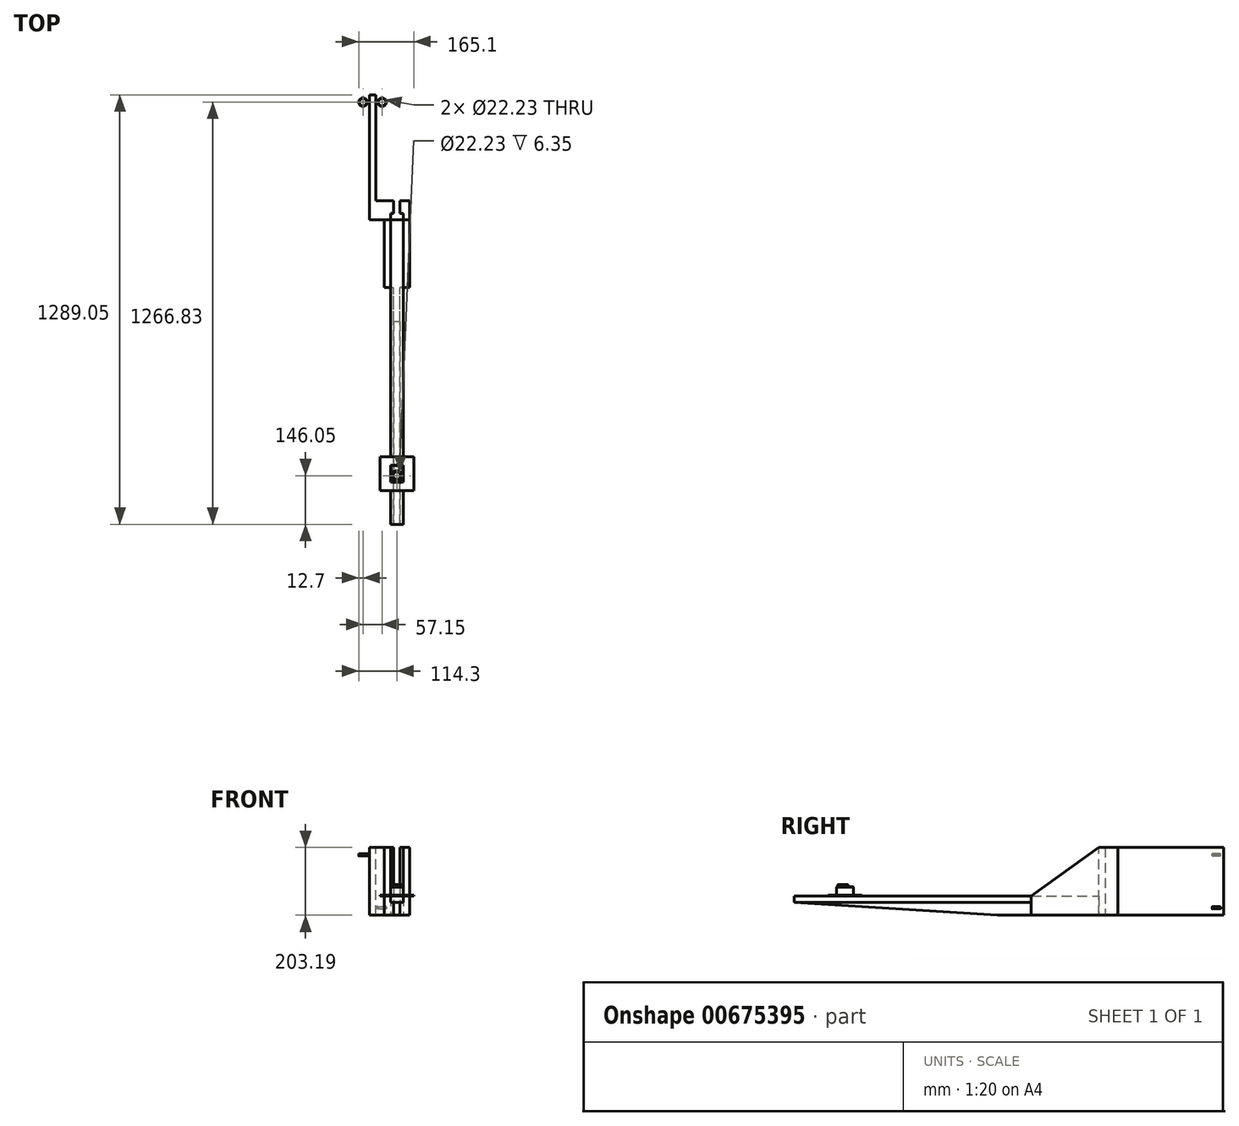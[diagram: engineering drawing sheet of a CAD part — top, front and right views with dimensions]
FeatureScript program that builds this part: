
annotation { "Feature Type Name" : "Feature", "Feature Type Description" : "" }
export const myFeature = defineFeature(function(context is Context, id is Id, definition is map)
    precondition{}
    {
        {
            var Q0;
            Q0=qCreatedBy(makeId("Front.planeOp"),FACE);
            var sketch = newSketch(context, id + "F0", { "sketchPlane" : qUnion([Q0])});
            skLineSegment(sketch, "E0.bottom", {"start": v(-19.05, 9.52) * mm, "end": v(19.05, 9.52) * mm});
            skLineSegment(sketch, "E0.top", {"start": v(-19.05, -9.53) * mm, "end": v(19.05, -9.53) * mm});
            skLineSegment(sketch, "E0.left", {"start": v(-19.05, 9.53) * mm, "end": v(-19.05, -9.53) * mm});
            skLineSegment(sketch, "E0.right", {"start": v(19.05, 9.53) * mm, "end": v(19.05, -9.53) * mm});
            skLineSegment(sketch, "E1.bottom", {"start": v(-9.52, -9.53) * mm, "end": v(9.53, -9.53) * mm});
            skLineSegment(sketch, "E1.top", {"start": v(-9.52, -47.62) * mm, "end": v(9.53, -47.62) * mm});
            skLineSegment(sketch, "E1.left", {"start": v(-9.52, -9.53) * mm, "end": v(-9.52, -47.62) * mm});
            skLineSegment(sketch, "E1.right", {"start": v(9.53, -9.52) * mm, "end": v(9.53, -47.62) * mm});
            skSolve(sketch);
        }
        {
            var Q0;
            Q0 = qSketchRegion(id + "F0", true);
            extrude(context, id + "F1", {"entities" : qUnion([Q0]), "depth" : 914.4 * mm, "offsetDistance" : 25.4 * mm});
        }
        {
            var Q0;
            Q0=makeQuery(id+"F1.opExtrude","SWEPT_FACE",FACE,{"disambiguationData":[OSD([sQuery(id+"F0.wireOp",EDGE,"E1.right")])]});
            var sketch = newSketch(context, id + "F2", { "sketchPlane" : qUnion([Q0])});
            skLineSegment(sketch, "E2", {"start": v(-914.4, -9.53) * mm, "end": v(-914.4, -47.62) * mm});
            skLineSegment(sketch, "E3", {"start": v(-914.4, -47.62) * mm, "end": v(-304.8, -47.62) * mm});
            skLineSegment(sketch, "E4", {"start": v(-304.8, -47.63) * mm, "end": v(-914.4, -9.53) * mm});
            skSolve(sketch);
        }
        {
            var Q0;
            Q0 = qSketchRegion(id + "F2", true);
            var Q1;
            Q1=makeQuery(id+"F2.imprint","IMPRINT",FACE,{"disambiguationData":[TD([[makeQuery(id+"F2.imprint","IMPRINT",EDGE,{"derivedFrom":sQuery(id+"F2.wireOp",EDGE,"E2")}),1.0]])]});
            extrude(context, id + "F3", {"entities" : qUnion([Q0, Q1]), "operationType" : NewBodyOperationType.REMOVE, "oppositeDirection" : true, "depth" : 25.4 * mm, "offsetDistance" : 25.4 * mm});
        }
        {
            var Q0;
            Q0=makeQuery(id+"F1.opExtrude","SWEPT_FACE",FACE,{"disambiguationData":[OSD([sQuery(id+"F0.wireOp",EDGE,"E0.bottom")])]});
            var sketch = newSketch(context, id + "F4", { "sketchPlane" : qUnion([Q0])});
            skLineSegment(sketch, "E5.bottom", {"start": v(-50.8, -711.2) * mm, "end": v(50.8, -711.2) * mm});
            skLineSegment(sketch, "E5.top", {"start": v(-50.8, -812.8) * mm, "end": v(50.8, -812.8) * mm});
            skLineSegment(sketch, "E5.left", {"start": v(-50.8, -711.2) * mm, "end": v(-50.8, -812.8) * mm});
            skLineSegment(sketch, "E5.right", {"start": v(50.8, -711.2) * mm, "end": v(50.8, -812.8) * mm});
            skSolve(sketch);
        }
        {
            var Q0;
            Q0 = qSketchRegion(id + "F4", true);
            extrude(context, id + "F5", {"entities" : qUnion([Q0]), "operationType" : NewBodyOperationType.ADD, "depth" : 3.17 * mm, "offsetDistance" : 25.4 * mm});
        }
        {
            var Q0;
            Q0=makeQuery(id+"F5.opExtrude","CAP_FACE",FACE,{"disambiguationData":[OSD([sQuery(id+"F4.wireOp",EDGE,"E5.bottom"),sQuery(id+"F4.wireOp",EDGE,"E5.top"),sQuery(id+"F4.wireOp",EDGE,"E5.left"),sQuery(id+"F4.wireOp",EDGE,"E5.right")])],"isStart":false});
            var sketch = newSketch(context, id + "F6", { "sketchPlane" : qUnion([Q0])});
            skLineSegment(sketch, "E6.bottom", {"start": v(-19.05, -736.6) * mm, "end": v(19.05, -736.6) * mm});
            skLineSegment(sketch, "E6.top", {"start": v(-19.05, -787.4) * mm, "end": v(19.05, -787.4) * mm});
            skLineSegment(sketch, "E6.left", {"start": v(-19.05, -736.6) * mm, "end": v(-19.05, -787.4) * mm});
            skLineSegment(sketch, "E6.right", {"start": v(19.05, -736.6) * mm, "end": v(19.05, -787.4) * mm});
            skSolve(sketch);
        }
        {
            var Q0;
            Q0=makeQuery(id+"F6.imprint","IMPRINT",FACE,{"disambiguationData":[TD([[makeQuery(id+"F6.imprint","IMPRINT",EDGE,{"derivedFrom":sQuery(id+"F6.wireOp",EDGE,"E6.bottom")}),-1.0]])]});
            extrude(context, id + "F7", {"entities" : qUnion([Q0]), "operationType" : NewBodyOperationType.ADD, "depth" : 25.4 * mm, "offsetDistance" : 25.4 * mm});
        }
        {
            var Q0;
            Q0=makeQuery(id+"F7.opExtrude","CAP_FACE",FACE,{"disambiguationData":[OSD([sQuery(id+"F6.wireOp",EDGE,"E6.bottom"),sQuery(id+"F6.wireOp",EDGE,"E6.top"),sQuery(id+"F6.wireOp",EDGE,"E6.left"),sQuery(id+"F6.wireOp",EDGE,"E6.right")])],"isStart":false});
            var sketch = newSketch(context, id + "F8", { "sketchPlane" : qUnion([Q0])});
            skCircle(sketch, "E7", {"center": v(0, -768.35) * mm, "radius": 15.24 * mm});
            skCircle(sketch, "E8", {"center": v(0, -768.35) * mm, "radius": 11.11 * mm});
            skSolve(sketch);
        }
        {
            var Q0;
            Q0 = qSketchRegion(id + "F8", true);
            extrude(context, id + "F9", {"entities" : qUnion([Q0]), "operationType" : NewBodyOperationType.ADD, "depth" : 6.35 * mm, "offsetDistance" : 25.4 * mm});
        }
        {
            var Q0;
            Q0=makeQuery(id+"F9.opExtrude","CAP_EDGE",EDGE,{"disambiguationData":[OSD([sQuery(id+"F8.wireOp",EDGE,"E7")])],"isStart":false});
            fillet(context, id + "F10", {"entities" : qUnion([Q0]), "radius" : 1.27 * mm, "tangentPropagation" : true, "allowEdgeOverflow" : false});
        }
        {
            var Q0;
            Q0=makeQuery(id+"F7.opExtrude","CAP_EDGE",EDGE,{"disambiguationData":[OSD([sQuery(id+"F6.wireOp",EDGE,"E6.right")])],"isStart":false});
            var Q1;
            Q1=makeQuery(id+"F7.opExtrude","CAP_EDGE",EDGE,{"disambiguationData":[OSD([sQuery(id+"F6.wireOp",EDGE,"E6.top")])],"isStart":false});
            var Q2;
            Q2=makeQuery(id+"F7.opExtrude","CAP_EDGE",EDGE,{"disambiguationData":[OSD([sQuery(id+"F6.wireOp",EDGE,"E6.left")])],"isStart":false});
            var Q3;
            Q3=makeQuery(id+"F7.opExtrude","CAP_EDGE",EDGE,{"disambiguationData":[OSD([sQuery(id+"F6.wireOp",EDGE,"E6.bottom")])],"isStart":false});
            chamfer(context, id + "F11", {"entities" : qUnion([Q0, Q1, Q2, Q3]), "width" : 1.27 * mm, "tangentPropagation" : true});
        }
        {
            var Q0;
            Q0=makeQuery(id+"F1.opExtrude","SWEPT_FACE",FACE,{"disambiguationData":[OSD([sQuery(id+"F0.wireOp",EDGE,"E0.right")])]});
            var sketch = newSketch(context, id + "F12", { "sketchPlane" : qUnion([Q0])});
            skLineSegment(sketch, "E9", {"start": v(-203.2, 9.52) * mm, "end": v(0, 155.58) * mm});
            skLineSegment(sketch, "E10", {"start": v(0, 155.58) * mm, "end": v(57.15, 155.58) * mm});
            skLineSegment(sketch, "E11", {"start": v(57.15, 155.58) * mm, "end": v(57.15, -47.62) * mm});
            skLineSegment(sketch, "E12", {"start": v(57.15, -47.62) * mm, "end": v(-203.2, -47.63) * mm});
            skLineSegment(sketch, "E13", {"start": v(-203.2, -47.63) * mm, "end": v(-203.2, 9.52) * mm});
            skSolve(sketch);
        }
        {
            var Q0;
            Q0 = qSketchRegion(id + "F12", true);
            extrude(context, id + "F13", {"entities" : qUnion([Q0]), "operationType" : NewBodyOperationType.ADD, "depth" : 19.05 * mm, "offsetDistance" : 25.4 * mm});
        }
        {
            var Q0;
            Q0=makeQuery(id+"F1.opExtrude","SWEPT_FACE",FACE,{"disambiguationData":[OSD([sQuery(id+"F0.wireOp",EDGE,"E0.left")])]});
            var sketch = newSketch(context, id + "F14", { "sketchPlane" : qUnion([Q0])});
            skLineSegment(sketch, "E14", {"start": v(-57.15, -47.63) * mm, "end": v(-57.15, 155.57) * mm});
            skLineSegment(sketch, "E15", {"start": v(-57.15, 155.57) * mm, "end": v(0, 155.57) * mm});
            skLineSegment(sketch, "E16", {"start": v(0, 155.57) * mm, "end": v(203.2, 9.53) * mm});
            skLineSegment(sketch, "E17", {"start": v(203.2, 9.52) * mm, "end": v(203.2, -47.63) * mm});
            skLineSegment(sketch, "E18", {"start": v(203.2, -47.63) * mm, "end": v(-57.15, -47.63) * mm});
            skSolve(sketch);
        }
        {
            var Q0;
            Q0 = qSketchRegion(id + "F14", true);
            var Q1;
            Q1=makeQuery(id+"F14.imprint","IMPRINT",FACE,{"disambiguationData":[TD([[makeQuery(id+"F14.imprint","IMPRINT",EDGE,{"derivedFrom":sQuery(id+"F14.wireOp",EDGE,"E14")}),-1.0]])]});
            extrude(context, id + "F15", {"entities" : qUnion([Q0, Q1]), "operationType" : NewBodyOperationType.ADD, "depth" : 19.05 * mm, "offsetDistance" : 25.4 * mm});
        }
        {
            var Q0;
            Q0=makeQuery(id+"F1.opExtrude","CAP_FACE",FACE,{"disambiguationData":[OSD([sQuery(id+"F0.wireOp",EDGE,"E0.bottom"),sQuery(id+"F0.wireOp",EDGE,"E0.top"),sQuery(id+"F0.wireOp",EDGE,"E0.left"),sQuery(id+"F0.wireOp",EDGE,"E0.right"),sQuery(id+"F0.wireOp",EDGE,"E1.top"),sQuery(id+"F0.wireOp",EDGE,"E1.left"),sQuery(id+"F0.wireOp",EDGE,"E1.right")])],"isStart":true});
            var sketch = newSketch(context, id + "F16", { "sketchPlane" : qUnion([Q0])});
            skLineSegment(sketch, "E19.bottom", {"start": v(-9.53, -9.53) * mm, "end": v(-19.05, -9.53) * mm});
            skLineSegment(sketch, "E19.top", {"start": v(-9.52, -47.62) * mm, "end": v(-19.05, -47.62) * mm});
            skLineSegment(sketch, "E19.left", {"start": v(-9.53, -9.53) * mm, "end": v(-9.53, -47.62) * mm});
            skLineSegment(sketch, "E19.right", {"start": v(-19.05, -9.53) * mm, "end": v(-19.05, -47.62) * mm});
            skLineSegment(sketch, "E20.bottom", {"start": v(9.52, -9.53) * mm, "end": v(19.05, -9.53) * mm});
            skLineSegment(sketch, "E20.top", {"start": v(9.53, -47.62) * mm, "end": v(19.05, -47.62) * mm});
            skLineSegment(sketch, "E20.left", {"start": v(9.52, -9.53) * mm, "end": v(9.52, -47.62) * mm});
            skLineSegment(sketch, "E20.right", {"start": v(19.05, -9.53) * mm, "end": v(19.05, -47.62) * mm});
            skSolve(sketch);
        }
        {
            var Q0;
            Q0 = qSketchRegion(id + "F16", true);
            extrude(context, id + "F17", {"entities" : qUnion([Q0]), "operationType" : NewBodyOperationType.ADD, "oppositeDirection" : true, "depth" : 203.2 * mm, "offsetDistance" : 25.4 * mm});
        }
        {
            var Q0;
            Q0=makeQuery(id+"F17.boolean.opBoolean","MERGE",FACE,{"derivedFrom":[makeQuery(id+"F1.opExtrude","SWEPT_FACE",FACE,{"disambiguationData":[OSD([sQuery(id+"F0.wireOp",EDGE,"E1.top")])]}),makeQuery(id+"F13.opExtrude","SWEPT_FACE",FACE,{"disambiguationData":[OSD([sQuery(id+"F12.wireOp",EDGE,"E12")])]}),makeQuery(id+"F15.opExtrude","SWEPT_FACE",FACE,{"disambiguationData":[OSD([sQuery(id+"F14.wireOp",EDGE,"E18")])]}),makeQuery(id+"F17.opExtrude","SWEPT_FACE",FACE,{"disambiguationData":[OSD([sQuery(id+"F16.wireOp",EDGE,"E19.top")])]}),makeQuery(id+"F17.opExtrude","SWEPT_FACE",FACE,{"disambiguationData":[OSD([sQuery(id+"F16.wireOp",EDGE,"E20.top")])]})]});
            var sketch = newSketch(context, id + "F18", { "sketchPlane" : qUnion([Q0])});
            skLineSegment(sketch, "E21.bottom", {"start": v(-19.05, -19.05) * mm, "end": v(-9.52, -19.05) * mm});
            skLineSegment(sketch, "E21.top", {"start": v(-19.05, -57.15) * mm, "end": v(-9.52, -57.15) * mm});
            skLineSegment(sketch, "E21.left", {"start": v(-19.05, -19.05) * mm, "end": v(-19.05, -57.15) * mm});
            skLineSegment(sketch, "E21.right", {"start": v(-9.52, -19.05) * mm, "end": v(-9.52, -57.15) * mm});
            skLineSegment(sketch, "E22.bottom", {"start": v(19.05, -19.05) * mm, "end": v(9.53, -19.05) * mm});
            skLineSegment(sketch, "E22.top", {"start": v(19.05, -57.15) * mm, "end": v(9.53, -57.15) * mm});
            skLineSegment(sketch, "E22.left", {"start": v(19.05, -19.05) * mm, "end": v(19.05, -57.15) * mm});
            skLineSegment(sketch, "E22.right", {"start": v(9.53, -19.05) * mm, "end": v(9.53, -57.15) * mm});
            skSolve(sketch);
        }
        {
            var Q0;
            Q0 = qSketchRegion(id + "F18", true);
            extrude(context, id + "F19", {"entities" : qUnion([Q0]), "operationType" : NewBodyOperationType.ADD, "oppositeDirection" : true, "depth" : 203.2 * mm, "offsetDistance" : 25.4 * mm});
        }
        {
            var Q0;
            Q0=makeQuery(id+"F19.boolean.opBoolean","MERGE",FACE,{"derivedFrom":[makeQuery(id+"F15.opExtrude","SWEPT_FACE",FACE,{"disambiguationData":[OSD([sQuery(id+"F14.wireOp",EDGE,"E15")])]}),makeQuery(id+"F19.opExtrude","CAP_FACE",FACE,{"disambiguationData":[OSD([sQuery(id+"F18.wireOp",EDGE,"E21.bottom"),sQuery(id+"F18.wireOp",EDGE,"E21.top"),sQuery(id+"F18.wireOp",EDGE,"E21.left"),sQuery(id+"F18.wireOp",EDGE,"E21.right")])],"isStart":false})]});
            var sketch = newSketch(context, id + "F20", { "sketchPlane" : qUnion([Q0])});
            skLineSegment(sketch, "E23.bottom", {"start": v(-38.1, 57.15) * mm, "end": v(-63.5, 57.15) * mm});
            skLineSegment(sketch, "E23.top", {"start": v(-38.1, 0) * mm, "end": v(-63.5, 0) * mm});
            skLineSegment(sketch, "E23.left", {"start": v(-38.1, 57.15) * mm, "end": v(-38.1, 0) * mm});
            skLineSegment(sketch, "E23.right", {"start": v(-63.5, 57.15) * mm, "end": v(-63.5, 0) * mm});
            skSolve(sketch);
        }
        {
            var Q0;
            Q0 = qSketchRegion(id + "F20", true);
            extrude(context, id + "F21", {"entities" : qUnion([Q0]), "operationType" : NewBodyOperationType.ADD, "oppositeDirection" : true, "depth" : 203.2 * mm, "offsetDistance" : 25.4 * mm});
        }
        {
            var Q0;
            Q0=makeQuery(id+"F21.boolean.opBoolean","MERGE",FACE,{"derivedFrom":[makeQuery(id+"F19.boolean.opBoolean","MERGE",FACE,{"derivedFrom":[makeQuery(id+"F15.opExtrude","SWEPT_FACE",FACE,{"disambiguationData":[OSD([sQuery(id+"F14.wireOp",EDGE,"E15")])]}),makeQuery(id+"F19.opExtrude","CAP_FACE",FACE,{"disambiguationData":[OSD([sQuery(id+"F18.wireOp",EDGE,"E21.bottom"),sQuery(id+"F18.wireOp",EDGE,"E21.top"),sQuery(id+"F18.wireOp",EDGE,"E21.left"),sQuery(id+"F18.wireOp",EDGE,"E21.right")])],"isStart":false})]}),makeQuery(id+"F21.opExtrude","CAP_FACE",FACE,{"disambiguationData":[OSD([sQuery(id+"F20.wireOp",EDGE,"E23.bottom"),sQuery(id+"F20.wireOp",EDGE,"E23.top"),sQuery(id+"F20.wireOp",EDGE,"E23.left"),sQuery(id+"F20.wireOp",EDGE,"E23.right")])],"isStart":true})]});
            var sketch = newSketch(context, id + "F22", { "sketchPlane" : qUnion([Q0])});
            skLineSegment(sketch, "E24.bottom", {"start": v(-63.5, 0) * mm, "end": v(-82.55, 0) * mm});
            skLineSegment(sketch, "E24.top", {"start": v(-63.5, 374.65) * mm, "end": v(-82.55, 374.65) * mm});
            skLineSegment(sketch, "E24.left", {"start": v(-63.5, 0) * mm, "end": v(-63.5, 374.65) * mm});
            skLineSegment(sketch, "E24.right", {"start": v(-82.55, 0) * mm, "end": v(-82.55, 374.65) * mm});
            skSolve(sketch);
        }
        {
            var Q0;
            Q0 = qSketchRegion(id + "F22", true);
            extrude(context, id + "F23", {"entities" : qUnion([Q0]), "operationType" : NewBodyOperationType.ADD, "oppositeDirection" : true, "depth" : 203.2 * mm, "offsetDistance" : 25.4 * mm});
        }
        {
            var Q0;
            Q0=makeQuery(id+"F23.boolean.opBoolean","MERGE",FACE,{"derivedFrom":[makeQuery(id+"F21.boolean.opBoolean","MERGE",FACE,{"derivedFrom":[makeQuery(id+"F19.boolean.opBoolean","MERGE",FACE,{"derivedFrom":[makeQuery(id+"F15.opExtrude","SWEPT_FACE",FACE,{"disambiguationData":[OSD([sQuery(id+"F14.wireOp",EDGE,"E15")])]}),makeQuery(id+"F19.opExtrude","CAP_FACE",FACE,{"disambiguationData":[OSD([sQuery(id+"F18.wireOp",EDGE,"E21.bottom"),sQuery(id+"F18.wireOp",EDGE,"E21.top"),sQuery(id+"F18.wireOp",EDGE,"E21.left"),sQuery(id+"F18.wireOp",EDGE,"E21.right")])],"isStart":false})]}),makeQuery(id+"F21.opExtrude","CAP_FACE",FACE,{"disambiguationData":[OSD([sQuery(id+"F20.wireOp",EDGE,"E23.bottom"),sQuery(id+"F20.wireOp",EDGE,"E23.top"),sQuery(id+"F20.wireOp",EDGE,"E23.left"),sQuery(id+"F20.wireOp",EDGE,"E23.right")])],"isStart":true})]}),makeQuery(id+"F23.opExtrude","CAP_FACE",FACE,{"disambiguationData":[OSD([sQuery(id+"F22.wireOp",EDGE,"E24.bottom"),sQuery(id+"F22.wireOp",EDGE,"E24.top"),sQuery(id+"F22.wireOp",EDGE,"E24.left"),sQuery(id+"F22.wireOp",EDGE,"E24.right")])],"isStart":true})]});
            var sketch = newSketch(context, id + "F24", { "sketchPlane" : qUnion([Q0])});
            skLineSegment(sketch, "E25.MirrorCS", {"start": v(-89.3, 349.25) * mm, "end": v(-63.5, 349.25) * mm});
            skCircle(sketch, "E26.MirrorC", {"center": v(-101.6, 352.43) * mm, "radius": 11.11 * mm});
            skArc(sketch, "E27.MirrorCS", {"start": v(-89.3, 349.25) * mm, "mid": v(-114.3, 352.43) * mm, "end": v(-89.3, 355.6) * mm});
            skLineSegment(sketch, "E28.MirrorCS", {"start": v(-63.5, 355.6) * mm, "end": v(-63.5, 349.25) * mm});
            skLineSegment(sketch, "E29.MirrorCS", {"start": v(-89.3, 355.6) * mm, "end": v(-63.5, 355.6) * mm});
            skSolve(sketch);
        }
        {
            var Q0;
            Q0 = qSketchRegion(id + "F24", true);
            extrude(context, id + "F25", {"entities" : qUnion([Q0]), "operationType" : NewBodyOperationType.ADD, "oppositeDirection" : true, "depth" : 25.4 * mm, "offsetDistance" : 25.4 * mm, "hasSecondDirection" : true, "secondDirectionOppositeDirection" : true, "secondDirectionDepth" : 19.05 * mm});
        }
        {
            var Q0;
            Q0=makeQuery(id+"F25.opExtrude","CAP_EDGE",EDGE,{"disambiguationData":[OSD([sQuery(id+"F24.wireOp",EDGE,"E29.MirrorCS")])],"isStart":true});
            var Q1;
            Q1=makeQuery(id+"F25.opExtrude","CAP_EDGE",EDGE,{"disambiguationData":[OSD([sQuery(id+"F24.wireOp",EDGE,"E25.MirrorCS")])],"isStart":true});
            var Q2;
            Q2=makeQuery(id+"F25.opExtrude","CAP_EDGE",EDGE,{"disambiguationData":[OSD([sQuery(id+"F24.wireOp",EDGE,"E29.MirrorCS")])],"isStart":false});
            var Q3;
            Q3=makeQuery(id+"F25.opExtrude","CAP_EDGE",EDGE,{"disambiguationData":[OSD([sQuery(id+"F24.wireOp",EDGE,"E25.MirrorCS")])],"isStart":false});
            fillet(context, id + "F26", {"entities" : qUnion([Q0, Q1, Q2, Q3]), "radius" : 3.17 * mm, "tangentPropagation" : true, "allowEdgeOverflow" : false});
        }
        {
            var Q0;
            Q0=makeQuery(id+"F25.opExtrude","CAP_EDGE",EDGE,{"disambiguationData":[OSD([sQuery(id+"F24.wireOp",EDGE,"E26.MirrorC")])],"isStart":true});
            var Q1;
            Q1=makeQuery(id+"F25.opExtrude","CAP_EDGE",EDGE,{"disambiguationData":[OSD([sQuery(id+"F24.wireOp",EDGE,"E26.MirrorC")])],"isStart":false});
            var Q2;
            Q2=makeQuery(id+"F25.opExtrude","CAP_EDGE",EDGE,{"disambiguationData":[OSD([sQuery(id+"F24.wireOp",EDGE,"E27.MirrorCS")])],"isStart":false});
            var Q3;
            Q3=makeQuery(id+"F25.opExtrude","CAP_EDGE",EDGE,{"disambiguationData":[OSD([sQuery(id+"F24.wireOp",EDGE,"E27.MirrorCS")])],"isStart":true});
            fillet(context, id + "F27", {"entities" : qUnion([Q0, Q1, Q2, Q3]), "radius" : 0.64 * mm, "tangentPropagation" : true, "allowEdgeOverflow" : false});
        }
        {
            var Q0;
            Q0=makeQuery(id+"F23.boolean.opBoolean","MERGE",FACE,{"derivedFrom":[makeQuery(id+"F21.boolean.opBoolean","MERGE",FACE,{"derivedFrom":[makeQuery(id+"F19.boolean.opBoolean","MERGE",FACE,{"derivedFrom":[makeQuery(id+"F17.boolean.opBoolean","MERGE",FACE,{"derivedFrom":[makeQuery(id+"F1.opExtrude","SWEPT_FACE",FACE,{"disambiguationData":[OSD([sQuery(id+"F0.wireOp",EDGE,"E1.top")])]}),makeQuery(id+"F13.opExtrude","SWEPT_FACE",FACE,{"disambiguationData":[OSD([sQuery(id+"F12.wireOp",EDGE,"E12")])]}),makeQuery(id+"F15.opExtrude","SWEPT_FACE",FACE,{"disambiguationData":[OSD([sQuery(id+"F14.wireOp",EDGE,"E18")])]}),makeQuery(id+"F17.opExtrude","SWEPT_FACE",FACE,{"disambiguationData":[OSD([sQuery(id+"F16.wireOp",EDGE,"E19.top")])]}),makeQuery(id+"F17.opExtrude","SWEPT_FACE",FACE,{"disambiguationData":[OSD([sQuery(id+"F16.wireOp",EDGE,"E20.top")])]})]}),makeQuery(id+"F19.opExtrude","CAP_FACE",FACE,{"disambiguationData":[OSD([sQuery(id+"F18.wireOp",EDGE,"E21.bottom"),sQuery(id+"F18.wireOp",EDGE,"E21.top"),sQuery(id+"F18.wireOp",EDGE,"E21.left"),sQuery(id+"F18.wireOp",EDGE,"E21.right")])],"isStart":true}),makeQuery(id+"F19.opExtrude","CAP_FACE",FACE,{"disambiguationData":[OSD([sQuery(id+"F18.wireOp",EDGE,"E22.bottom"),sQuery(id+"F18.wireOp",EDGE,"E22.top"),sQuery(id+"F18.wireOp",EDGE,"E22.left"),sQuery(id+"F18.wireOp",EDGE,"E22.right")])],"isStart":true})]}),makeQuery(id+"F21.opExtrude","CAP_FACE",FACE,{"disambiguationData":[OSD([sQuery(id+"F20.wireOp",EDGE,"E23.bottom"),sQuery(id+"F20.wireOp",EDGE,"E23.top"),sQuery(id+"F20.wireOp",EDGE,"E23.left"),sQuery(id+"F20.wireOp",EDGE,"E23.right")])],"isStart":false})]}),makeQuery(id+"F23.opExtrude","CAP_FACE",FACE,{"disambiguationData":[OSD([sQuery(id+"F22.wireOp",EDGE,"E24.bottom"),sQuery(id+"F22.wireOp",EDGE,"E24.top"),sQuery(id+"F22.wireOp",EDGE,"E24.left"),sQuery(id+"F22.wireOp",EDGE,"E24.right")])],"isStart":false})]});
            var sketch = newSketch(context, id + "F28", { "sketchPlane" : qUnion([Q0])});
            skArc(sketch, "E30.MirrorCS", {"start": v(-56.75, -349.25) * mm, "mid": v(-31.75, -352.43) * mm, "end": v(-56.75, -355.6) * mm});
            skLineSegment(sketch, "E31.MirrorCS", {"start": v(-82.55, -355.6) * mm, "end": v(-82.55, -349.25) * mm});
            skLineSegment(sketch, "E32.MirrorCS", {"start": v(-56.75, -355.6) * mm, "end": v(-82.55, -355.6) * mm});
            skLineSegment(sketch, "E33.MirrorCS", {"start": v(-56.75, -349.25) * mm, "end": v(-82.55, -349.25) * mm});
            skCircle(sketch, "E34.MirrorC", {"center": v(-44.45, -352.43) * mm, "radius": 11.11 * mm});
            skLineSegment(sketch, "E35.MirrorCS", {"start": v(194.26, -482.87) * mm, "end": v(168.46, -482.87) * mm});
            skSolve(sketch);
        }
        {
            var Q0;
            Q0 = qSketchRegion(id + "F28", true);
            extrude(context, id + "F29", {"entities" : qUnion([Q0]), "operationType" : NewBodyOperationType.ADD, "oppositeDirection" : true, "depth" : 25.4 * mm, "offsetDistance" : 25.4 * mm, "hasSecondDirection" : true, "secondDirectionOppositeDirection" : true, "secondDirectionDepth" : 19.05 * mm});
        }
        {
            var Q0;
            Q0=makeQuery(id+"F29.opExtrude","CAP_EDGE",EDGE,{"disambiguationData":[OSD([sQuery(id+"F28.wireOp",EDGE,"E33.MirrorCS")])],"isStart":true});
            var Q1;
            Q1=makeQuery(id+"F29.opExtrude","CAP_EDGE",EDGE,{"disambiguationData":[OSD([sQuery(id+"F28.wireOp",EDGE,"E32.MirrorCS")])],"isStart":true});
            var Q2;
            Q2=makeQuery(id+"F29.opExtrude","CAP_EDGE",EDGE,{"disambiguationData":[OSD([sQuery(id+"F28.wireOp",EDGE,"E33.MirrorCS")])],"isStart":false});
            var Q3;
            Q3=makeQuery(id+"F29.opExtrude","CAP_EDGE",EDGE,{"disambiguationData":[OSD([sQuery(id+"F28.wireOp",EDGE,"E32.MirrorCS")])],"isStart":false});
            fillet(context, id + "F30", {"entities" : qUnion([Q0, Q1, Q2, Q3]), "radius" : 3.17 * mm, "tangentPropagation" : true, "allowEdgeOverflow" : false});
        }
        {
            var Q0;
            Q0=makeQuery(id+"F29.opExtrude","CAP_EDGE",EDGE,{"disambiguationData":[OSD([sQuery(id+"F28.wireOp",EDGE,"E34.MirrorC")])],"isStart":false});
            var Q1;
            Q1=makeQuery(id+"F29.opExtrude","CAP_EDGE",EDGE,{"disambiguationData":[OSD([sQuery(id+"F28.wireOp",EDGE,"E34.MirrorC")])],"isStart":true});
            var Q2;
            Q2=makeQuery(id+"F29.opExtrude","CAP_EDGE",EDGE,{"disambiguationData":[OSD([sQuery(id+"F28.wireOp",EDGE,"E30.MirrorCS")])],"isStart":false});
            var Q3;
            Q3=makeQuery(id+"F29.opExtrude","CAP_EDGE",EDGE,{"disambiguationData":[OSD([sQuery(id+"F28.wireOp",EDGE,"E30.MirrorCS")])],"isStart":true});
            fillet(context, id + "F31", {"entities" : qUnion([Q0, Q1, Q2, Q3]), "radius" : 0.64 * mm, "tangentPropagation" : true, "allowEdgeOverflow" : false});
        }
    });
